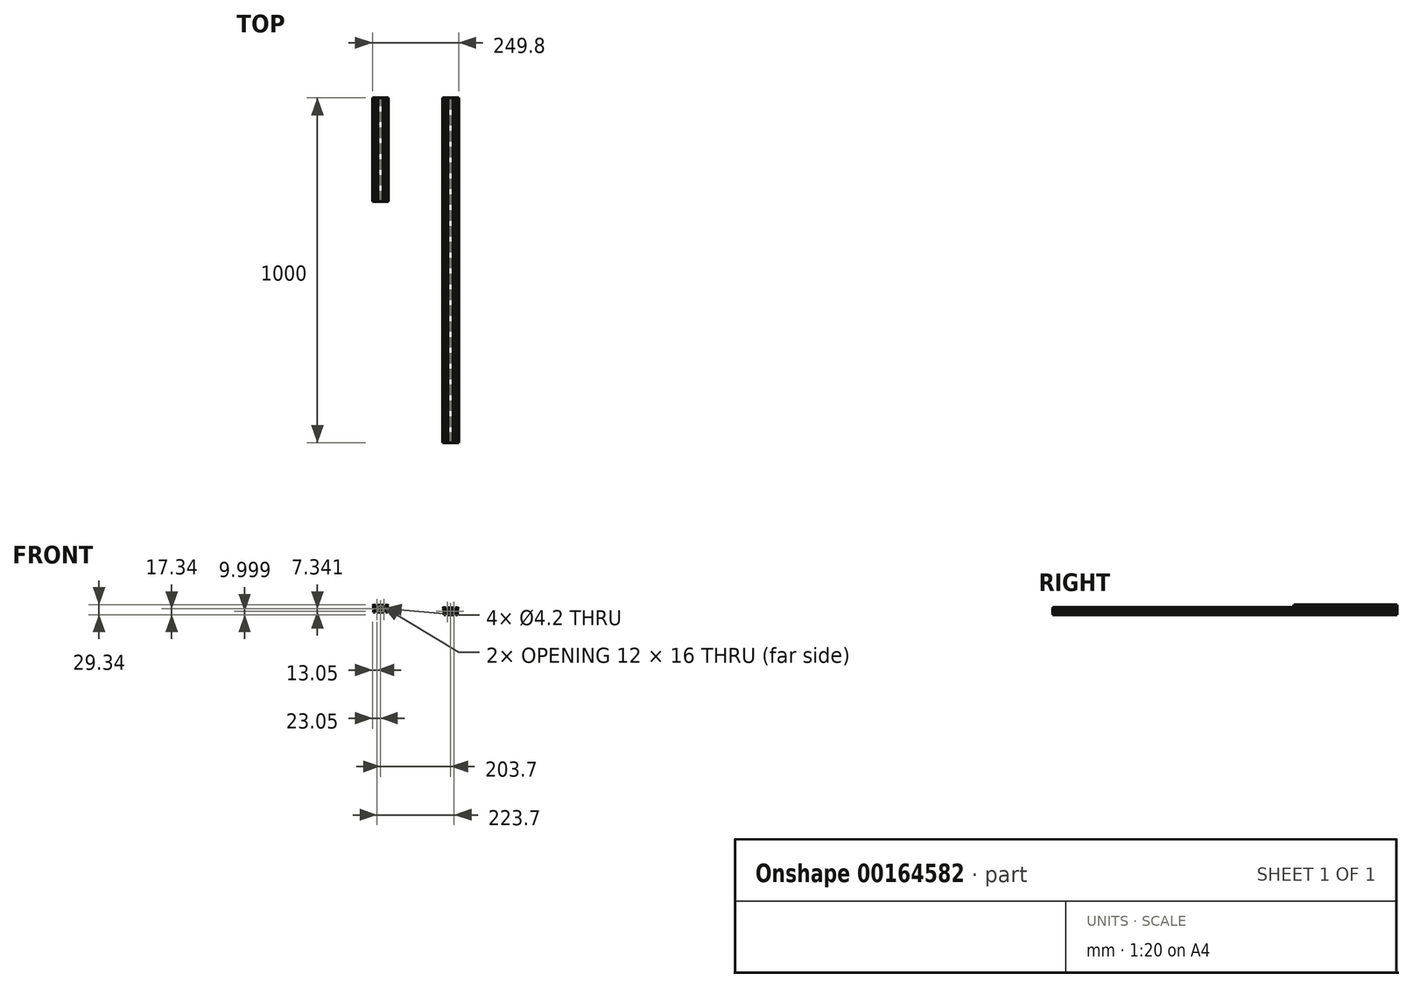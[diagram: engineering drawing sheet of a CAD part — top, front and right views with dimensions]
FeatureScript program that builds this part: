
annotation { "Feature Type Name" : "Feature", "Feature Type Description" : "" }
export const myFeature = defineFeature(function(context is Context, id is Id, definition is map)
    precondition{}
    {
        {
            var Q0;
            Q0=qCreatedBy(makeId("Front.planeOp"),FACE);
            var sketch = newSketch(context, id + "F0", { "sketchPlane" : qUnion([Q0])});
            skLineSegment(sketch, "E0.bottom", {"start": v(-20, 10) * mm, "end": v(-13.5, 10) * mm});
            skLineSegment(sketch, "E0.left", {"start": v(-20, 6.63) * mm, "end": v(-20, 3) * mm});
            skLineSegment(sketch, "E1.bottom", {"start": v(-20.37, 12) * mm, "end": v(-20, 12) * mm});
            skLineSegment(sketch, "E2", {"start": v(-20, 10) * mm, "end": v(-20, 12) * mm});
            skPoint(sketch, "E3.endSnap0", {"position": v(0, -10) * mm});
            skLineSegment(sketch, "E4", {"start": v(-23.05, 9.32) * mm, "end": v(-20.37, 12) * mm});
            skLineSegment(sketch, "E5", {"start": v(-23.05, 9.32) * mm, "end": v(-20.37, 6.63) * mm});
            skLineSegment(sketch, "E6", {"start": v(-20.37, 6.63) * mm, "end": v(-20, 6.63) * mm});
            skLineSegment(sketch, "E7.bottom", {"start": v(-2, 10) * mm, "end": v(-7.5, 10) * mm});
            skLineSegment(sketch, "E7.top", {"start": v(0, 8) * mm, "end": v(-2, 8) * mm});
            skLineSegment(sketch, "E7.left", {"start": v(0, 10) * mm, "end": v(0, 8) * mm});
            skLineSegment(sketch, "E7.right", {"start": v(-7.5, 10) * mm, "end": v(-7.5, 8) * mm});
            skLineSegment(sketch, "E8.top", {"start": v(-16, 8) * mm, "end": v(-13.5, 8) * mm});
            skLineSegment(sketch, "E8.right", {"start": v(-13.5, 10) * mm, "end": v(-13.5, 8) * mm});
            skLineSegment(sketch, "E9.bottom", {"start": v(-20, 10) * mm, "end": v(-18, 10) * mm});
            skLineSegment(sketch, "E9.top", {"start": v(-20, 3) * mm, "end": v(-18, 3) * mm});
            skLineSegment(sketch, "E9.right", {"start": v(-18, 6) * mm, "end": v(-18, 3) * mm});
            skLineSegment(sketch, "E10.top", {"start": v(-20, -3) * mm, "end": v(-18, -3) * mm});
            skLineSegment(sketch, "E11.bottom", {"start": v(-20, -10) * mm, "end": v(-15, -10) * mm});
            skLineSegment(sketch, "E11.left", {"start": v(-20, -10) * mm, "end": v(-20, -8) * mm});
            skLineSegment(sketch, "E11.right", {"start": v(-15, -10) * mm, "end": v(-15, -8) * mm});
            skCircle(sketch, "E12", {"center": v(-10, 0) * mm, "radius": 2.1 * mm});
            skLineSegment(sketch, "E13.bottom", {"start": v(-20, 10) * mm, "end": v(-16, 10) * mm});
            skLineSegment(sketch, "E13.top", {"start": v(-18, 6) * mm, "end": v(-17.41, 6) * mm});
            skLineSegment(sketch, "E13.right", {"start": v(-16, 8) * mm, "end": v(-16, 7.41) * mm});
            skLineSegment(sketch, "E14.right", {"start": v(-4, 8) * mm, "end": v(-4, 7.41) * mm});
            skLineSegment(sketch, "E15.top", {"start": v(-18, -6) * mm, "end": v(-17.41, -6) * mm});
            skLineSegment(sketch, "E15.left", {"start": v(-20, -10) * mm, "end": v(-20, -6) * mm});
            skLineSegment(sketch, "E15.right", {"start": v(-16, -8) * mm, "end": v(-16, -7.41) * mm});
            skLineSegment(sketch, "E16.bottom", {"start": v(-12.59, 4) * mm, "end": v(-7.41, 4) * mm});
            skLineSegment(sketch, "E16.top", {"start": v(-12.59, -4) * mm, "end": v(-7.41, -4) * mm});
            skLineSegment(sketch, "E16.left", {"start": v(-14, 2.59) * mm, "end": v(-14, -2.59) * mm});
            skLineSegment(sketch, "E16.right", {"start": v(-6, 2.59) * mm, "end": v(-6, -2.59) * mm});
            skLineSegment(sketch, "E17", {"start": v(-16, 7.41) * mm, "end": v(-12.59, 4) * mm});
            skLineSegment(sketch, "E18", {"start": v(-17.41, 6) * mm, "end": v(-14, 2.59) * mm});
            skPoint(sketch, "E19.orphan", {"position": v(-16, 6) * mm});
            skLineSegment(sketch, "E20.trimOffspring", {"start": v(-20, 6.63) * mm, "end": v(-20, 6) * mm});
            skLineSegment(sketch, "E21.trimOffspring", {"start": v(-20, -3) * mm, "end": v(-20, -10) * mm});
            skLineSegment(sketch, "E22.trimOffspring", {"start": v(-7.5, 10) * mm, "end": v(-4, 10) * mm});
            skLineSegment(sketch, "E23", {"start": v(-10, 10.96) * mm, "end": v(-10, -11.55) * mm, "construction": true});
            skLineSegment(sketch, "E24.MirrorCS", {"start": v(-4, 7.41) * mm, "end": v(-7.41, 4) * mm});
            skLineSegment(sketch, "E25.MirrorCS", {"start": v(-2.59, 6) * mm, "end": v(-6, 2.59) * mm});
            skLineSegment(sketch, "E26", {"start": v(-2, 8) * mm, "end": v(-2, 6.59) * mm});
            skLineSegment(sketch, "E27", {"start": v(-2.59, 6) * mm, "end": v(-2, 6.59) * mm});
            skLineSegment(sketch, "E28.trimOffspring", {"start": v(-4, 8) * mm, "end": v(-7.5, 8) * mm});
            skPoint(sketch, "E29.orphan", {"position": v(-2, 10) * mm});
            skPoint(sketch, "E30.orphan", {"position": v(-4, 10) * mm});
            skLineSegment(sketch, "E31.trimOffspring", {"start": v(-2, 10) * mm, "end": v(0, 10) * mm});
            skLineSegment(sketch, "E32", {"start": v(-21.49, 0) * mm, "end": v(3.6, 0) * mm, "construction": true});
            skLineSegment(sketch, "E33.MirrorCS", {"start": v(-17.41, -6) * mm, "end": v(-14, -2.59) * mm});
            skLineSegment(sketch, "E34.MirrorCS", {"start": v(-16, -7.41) * mm, "end": v(-12.59, -4) * mm});
            skLineSegment(sketch, "E35.MirrorCS", {"start": v(-4, -8) * mm, "end": v(-4, -7.41) * mm});
            skLineSegment(sketch, "E36.MirrorCS", {"start": v(-2.59, -6) * mm, "end": v(-2, -6.59) * mm});
            skLineSegment(sketch, "E37.MirrorCS", {"start": v(-4, -8) * mm, "end": v(-7.5, -8) * mm});
            skLineSegment(sketch, "E38.MirrorCS", {"start": v(0, -8) * mm, "end": v(-2, -8) * mm});
            skLineSegment(sketch, "E39.MirrorCS", {"start": v(0, -10) * mm, "end": v(0, -8) * mm});
            skLineSegment(sketch, "E40.MirrorCS", {"start": v(-2, -10) * mm, "end": v(-7.5, -10) * mm});
            skLineSegment(sketch, "E41.MirrorCS", {"start": v(-7.5, -10) * mm, "end": v(-7.5, -8) * mm});
            skLineSegment(sketch, "E42.MirrorCS", {"start": v(-2, -8) * mm, "end": v(-2, -6.59) * mm});
            skLineSegment(sketch, "E43.MirrorCS", {"start": v(-7.5, -10) * mm, "end": v(-4, -10) * mm});
            skLineSegment(sketch, "E44.MirrorCS", {"start": v(-2.59, -6) * mm, "end": v(-6, -2.59) * mm});
            skLineSegment(sketch, "E45.MirrorCS", {"start": v(-4, -7.41) * mm, "end": v(-7.41, -4) * mm});
            skLineSegment(sketch, "E46.trimOffspring", {"start": v(-18, -6) * mm, "end": v(-18, -3) * mm});
            skLineSegment(sketch, "E47.trimOffspring", {"start": v(-16, -8) * mm, "end": v(-15, -8) * mm});
            skLineSegment(sketch, "E48.trimOffspring", {"start": v(-7.5, -10) * mm, "end": v(-2, -10) * mm});
            skLineSegment(sketch, "E49.trimOffspring", {"start": v(-7.5, -10) * mm, "end": v(0, -10) * mm});
            skLineSegment(sketch, "E50.MirrorCS", {"start": v(4, -8) * mm, "end": v(4, -7.41) * mm});
            skLineSegment(sketch, "E51.MirrorCS", {"start": v(4, 8) * mm, "end": v(4, 7.41) * mm});
            skLineSegment(sketch, "E52.MirrorCS", {"start": v(20, 6.63) * mm, "end": v(20, 6) * mm});
            skLineSegment(sketch, "E53.MirrorCS", {"start": v(20.37, 6.63) * mm, "end": v(20, 6.63) * mm});
            skLineSegment(sketch, "E54.MirrorCS", {"start": v(16, 8) * mm, "end": v(16, 7.41) * mm});
            skLineSegment(sketch, "E55.MirrorCS", {"start": v(18, 6) * mm, "end": v(17.41, 6) * mm});
            skLineSegment(sketch, "E56.MirrorCS", {"start": v(2.59, 6) * mm, "end": v(2, 6.59) * mm});
            skLineSegment(sketch, "E57.MirrorCS", {"start": v(16, -8) * mm, "end": v(15, -8) * mm});
            skLineSegment(sketch, "E58.MirrorCS", {"start": v(20.37, 12) * mm, "end": v(20, 12) * mm});
            skLineSegment(sketch, "E59.MirrorCS", {"start": v(2, -8) * mm, "end": v(2, -6.59) * mm});
            skLineSegment(sketch, "E60.MirrorCS", {"start": v(18, -6) * mm, "end": v(17.41, -6) * mm});
            skLineSegment(sketch, "E61.MirrorCS", {"start": v(2, 8) * mm, "end": v(2, 6.59) * mm});
            skLineSegment(sketch, "E62.MirrorCS", {"start": v(2.59, -6) * mm, "end": v(2, -6.59) * mm});
            skLineSegment(sketch, "E63.MirrorCS", {"start": v(16, -8) * mm, "end": v(16, -7.41) * mm});
            skLineSegment(sketch, "E64.MirrorCS", {"start": v(20, -10) * mm, "end": v(20, -8) * mm});
            skLineSegment(sketch, "E65.MirrorCS", {"start": v(20, -10) * mm, "end": v(20, -6) * mm});
            skLineSegment(sketch, "E66.MirrorCS", {"start": v(20, 6.63) * mm, "end": v(20, 3) * mm});
            skLineSegment(sketch, "E67.MirrorCS", {"start": v(20, 10) * mm, "end": v(13.5, 10) * mm});
            skLineSegment(sketch, "E68.MirrorCS", {"start": v(20, 10) * mm, "end": v(18, 10) * mm});
            skLineSegment(sketch, "E69.MirrorCS", {"start": v(2, 10) * mm, "end": v(7.5, 10) * mm});
            skLineSegment(sketch, "E70.MirrorCS", {"start": v(7.5, -10) * mm, "end": v(4, -10) * mm});
            skLineSegment(sketch, "E71.MirrorCS", {"start": v(23.05, 9.32) * mm, "end": v(20.37, 6.63) * mm});
            skLineSegment(sketch, "E72.MirrorCS", {"start": v(2, -10) * mm, "end": v(7.5, -10) * mm});
            skLineSegment(sketch, "E73.MirrorCS", {"start": v(16, -7.41) * mm, "end": v(12.59, -4) * mm});
            skLineSegment(sketch, "E74.MirrorCS", {"start": v(7.5, -10) * mm, "end": v(2, -10) * mm});
            skLineSegment(sketch, "E75.MirrorCS", {"start": v(20, -10) * mm, "end": v(15, -10) * mm});
            skLineSegment(sketch, "E76.MirrorCS", {"start": v(7.5, -10) * mm, "end": v(0, -10) * mm});
            skLineSegment(sketch, "E77.MirrorCS", {"start": v(16, 7.41) * mm, "end": v(12.59, 4) * mm});
            skPoint(sketch, "E78.MirrorP", {"position": v(4, 10) * mm});
            skLineSegment(sketch, "E79.MirrorCS", {"start": v(14, 2.59) * mm, "end": v(14, -2.59) * mm});
            skLineSegment(sketch, "E80.MirrorCS", {"start": v(7.5, -10) * mm, "end": v(7.5, -8) * mm});
            skPoint(sketch, "E81.MirrorP", {"position": v(2, 10) * mm});
            skLineSegment(sketch, "E82.MirrorCS", {"start": v(2.59, 6) * mm, "end": v(6, 2.59) * mm});
            skPoint(sketch, "E83.MirrorP", {"position": v(16, 6) * mm});
            skLineSegment(sketch, "E84.MirrorCS", {"start": v(17.41, -6) * mm, "end": v(14, -2.59) * mm});
            skLineSegment(sketch, "E85.MirrorCS", {"start": v(18, 6) * mm, "end": v(18, 3) * mm});
            skLineSegment(sketch, "E86.MirrorCS", {"start": v(10, 10.96) * mm, "end": v(10, -11.55) * mm, "construction": true});
            skLineSegment(sketch, "E87.MirrorCS", {"start": v(20, -3) * mm, "end": v(20, -10) * mm});
            skLineSegment(sketch, "E88.MirrorCS", {"start": v(13.5, 10) * mm, "end": v(13.5, 8) * mm});
            skLineSegment(sketch, "E89.MirrorCS", {"start": v(20, 3) * mm, "end": v(18, 3) * mm});
            skLineSegment(sketch, "E90.MirrorCS", {"start": v(23.05, 9.32) * mm, "end": v(20.37, 12) * mm});
            skLineSegment(sketch, "E91.MirrorCS", {"start": v(12.59, 4) * mm, "end": v(7.41, 4) * mm});
            skLineSegment(sketch, "E92.MirrorCS", {"start": v(4, -7.41) * mm, "end": v(7.41, -4) * mm});
            skLineSegment(sketch, "E93.MirrorCS", {"start": v(0, 8) * mm, "end": v(2, 8) * mm});
            skLineSegment(sketch, "E94.MirrorCS", {"start": v(2, 10) * mm, "end": v(0, 10) * mm});
            skLineSegment(sketch, "E95.MirrorCS", {"start": v(4, -8) * mm, "end": v(7.5, -8) * mm});
            skCircle(sketch, "E96.MirrorC", {"center": v(10, 0) * mm, "radius": 2.1 * mm});
            skLineSegment(sketch, "E97.MirrorCS", {"start": v(17.41, 6) * mm, "end": v(14, 2.59) * mm});
            skLineSegment(sketch, "E98.MirrorCS", {"start": v(12.59, -4) * mm, "end": v(7.41, -4) * mm});
            skLineSegment(sketch, "E99.MirrorCS", {"start": v(6, 2.59) * mm, "end": v(6, -2.59) * mm});
            skLineSegment(sketch, "E100.MirrorCS", {"start": v(4, 7.41) * mm, "end": v(7.41, 4) * mm});
            skLineSegment(sketch, "E101.MirrorCS", {"start": v(7.5, 10) * mm, "end": v(4, 10) * mm});
            skLineSegment(sketch, "E102.MirrorCS", {"start": v(0, -8) * mm, "end": v(2, -8) * mm});
            skLineSegment(sketch, "E103.MirrorCS", {"start": v(7.5, 10) * mm, "end": v(7.5, 8) * mm});
            skLineSegment(sketch, "E104.MirrorCS", {"start": v(16, 8) * mm, "end": v(13.5, 8) * mm});
            skLineSegment(sketch, "E105.MirrorCS", {"start": v(4, 8) * mm, "end": v(7.5, 8) * mm});
            skLineSegment(sketch, "E106.MirrorCS", {"start": v(2.59, -6) * mm, "end": v(6, -2.59) * mm});
            skLineSegment(sketch, "E107.MirrorCS", {"start": v(18, -6) * mm, "end": v(18, -3) * mm});
            skLineSegment(sketch, "E108.MirrorCS", {"start": v(20, 10) * mm, "end": v(20, 12) * mm});
            skLineSegment(sketch, "E109.MirrorCS", {"start": v(15, -10) * mm, "end": v(15, -8) * mm});
            skLineSegment(sketch, "E110.MirrorCS", {"start": v(20, 10) * mm, "end": v(16, 10) * mm});
            skLineSegment(sketch, "E111.MirrorCS", {"start": v(20, -3) * mm, "end": v(18, -3) * mm});
            skSolve(sketch);
        }
        {
            var Q0;
            Q0 = qSketchRegion(id + "F0", true);
            extrude(context, id + "F1", {"entities" : qUnion([Q0]), "offsetDistance" : 25 * mm, "depth" : 300 * mm});
        }
        {
            var Q0;
            Q0=qCreatedBy(makeId("Front.planeOp"),FACE);
            var sketch = newSketch(context, id + "F2", { "sketchPlane" : qUnion([Q0])});
            skLineSegment(sketch, "E112.bottom", {"start": v(183.7, 2.66) * mm, "end": v(190.2, 2.66) * mm});
            skLineSegment(sketch, "E112.left", {"start": v(183.7, -0.71) * mm, "end": v(183.7, -4.34) * mm});
            skLineSegment(sketch, "E113.bottom", {"start": v(183.33, 4.66) * mm, "end": v(183.7, 4.66) * mm});
            skLineSegment(sketch, "E114", {"start": v(183.7, 2.66) * mm, "end": v(183.7, 4.66) * mm});
            skPoint(sketch, "E115.endSnap0", {"position": v(203.7, -17.34) * mm});
            skLineSegment(sketch, "E116", {"start": v(180.65, 1.97) * mm, "end": v(183.33, 4.66) * mm});
            skLineSegment(sketch, "E117", {"start": v(180.65, 1.97) * mm, "end": v(183.33, -0.71) * mm});
            skLineSegment(sketch, "E118", {"start": v(183.33, -0.71) * mm, "end": v(183.7, -0.71) * mm});
            skLineSegment(sketch, "E119.bottom", {"start": v(201.7, 2.66) * mm, "end": v(196.2, 2.66) * mm});
            skLineSegment(sketch, "E119.top", {"start": v(203.7, 0.66) * mm, "end": v(201.7, 0.66) * mm});
            skLineSegment(sketch, "E119.left", {"start": v(203.7, 2.66) * mm, "end": v(203.7, 0.66) * mm});
            skLineSegment(sketch, "E119.right", {"start": v(196.2, 2.66) * mm, "end": v(196.2, 0.66) * mm});
            skLineSegment(sketch, "E120.top", {"start": v(187.7, 0.66) * mm, "end": v(190.2, 0.66) * mm});
            skLineSegment(sketch, "E120.right", {"start": v(190.2, 2.66) * mm, "end": v(190.2, 0.66) * mm});
            skLineSegment(sketch, "E121.bottom", {"start": v(183.7, 2.66) * mm, "end": v(185.7, 2.66) * mm});
            skLineSegment(sketch, "E121.top", {"start": v(183.7, -4.34) * mm, "end": v(185.7, -4.34) * mm});
            skLineSegment(sketch, "E121.right", {"start": v(185.7, -1.34) * mm, "end": v(185.7, -4.34) * mm});
            skLineSegment(sketch, "E122.top", {"start": v(183.7, -10.34) * mm, "end": v(185.7, -10.34) * mm});
            skLineSegment(sketch, "E123.bottom", {"start": v(183.7, -17.34) * mm, "end": v(188.7, -17.34) * mm});
            skLineSegment(sketch, "E123.left", {"start": v(183.7, -17.34) * mm, "end": v(183.7, -15.34) * mm});
            skLineSegment(sketch, "E123.right", {"start": v(188.7, -17.34) * mm, "end": v(188.7, -15.34) * mm});
            skCircle(sketch, "E124", {"center": v(193.7, -7.34) * mm, "radius": 2.1 * mm});
            skLineSegment(sketch, "E125.bottom", {"start": v(183.7, 2.66) * mm, "end": v(187.7, 2.66) * mm});
            skLineSegment(sketch, "E125.top", {"start": v(185.7, -1.34) * mm, "end": v(186.29, -1.34) * mm});
            skLineSegment(sketch, "E125.right", {"start": v(187.7, 0.66) * mm, "end": v(187.7, 0.07) * mm});
            skLineSegment(sketch, "E126.right", {"start": v(199.7, 0.66) * mm, "end": v(199.7, 0.07) * mm});
            skLineSegment(sketch, "E127.top", {"start": v(185.7, -13.34) * mm, "end": v(186.29, -13.34) * mm});
            skLineSegment(sketch, "E127.left", {"start": v(183.7, -17.34) * mm, "end": v(183.7, -13.34) * mm});
            skLineSegment(sketch, "E127.right", {"start": v(187.7, -15.34) * mm, "end": v(187.7, -14.76) * mm});
            skLineSegment(sketch, "E128.bottom", {"start": v(191.11, -3.34) * mm, "end": v(196.29, -3.34) * mm});
            skLineSegment(sketch, "E128.top", {"start": v(191.11, -11.34) * mm, "end": v(196.29, -11.34) * mm});
            skLineSegment(sketch, "E128.left", {"start": v(189.7, -4.76) * mm, "end": v(189.7, -9.93) * mm});
            skLineSegment(sketch, "E128.right", {"start": v(197.7, -4.76) * mm, "end": v(197.7, -9.93) * mm});
            skLineSegment(sketch, "E129", {"start": v(187.7, 0.07) * mm, "end": v(191.11, -3.34) * mm});
            skLineSegment(sketch, "E130", {"start": v(186.29, -1.34) * mm, "end": v(189.7, -4.76) * mm});
            skPoint(sketch, "E131.orphan", {"position": v(187.7, -1.34) * mm});
            skLineSegment(sketch, "E132.trimOffspring", {"start": v(183.7, -0.71) * mm, "end": v(183.7, -1.34) * mm});
            skLineSegment(sketch, "E133.trimOffspring", {"start": v(183.7, -10.34) * mm, "end": v(183.7, -17.34) * mm});
            skLineSegment(sketch, "E134.trimOffspring", {"start": v(196.2, 2.66) * mm, "end": v(199.7, 2.66) * mm});
            skLineSegment(sketch, "E135", {"start": v(193.7, 3.62) * mm, "end": v(193.7, -18.9) * mm, "construction": true});
            skLineSegment(sketch, "E136.MirrorCS", {"start": v(199.7, 0.07) * mm, "end": v(196.29, -3.34) * mm});
            skLineSegment(sketch, "E137.MirrorCS", {"start": v(201.11, -1.34) * mm, "end": v(197.7, -4.76) * mm});
            skLineSegment(sketch, "E138", {"start": v(201.7, 0.66) * mm, "end": v(201.7, -0.76) * mm});
            skLineSegment(sketch, "E139", {"start": v(201.11, -1.34) * mm, "end": v(201.7, -0.76) * mm});
            skLineSegment(sketch, "E140.trimOffspring", {"start": v(199.7, 0.66) * mm, "end": v(196.2, 0.66) * mm});
            skPoint(sketch, "E141.orphan", {"position": v(201.7, 2.66) * mm});
            skPoint(sketch, "E142.orphan", {"position": v(199.7, 2.66) * mm});
            skLineSegment(sketch, "E143.trimOffspring", {"start": v(201.7, 2.66) * mm, "end": v(203.7, 2.66) * mm});
            skLineSegment(sketch, "E144", {"start": v(182.21, -7.34) * mm, "end": v(207.3, -7.34) * mm, "construction": true});
            skLineSegment(sketch, "E145.MirrorCS", {"start": v(186.29, -13.34) * mm, "end": v(189.7, -9.93) * mm});
            skLineSegment(sketch, "E146.MirrorCS", {"start": v(187.7, -14.76) * mm, "end": v(191.11, -11.34) * mm});
            skLineSegment(sketch, "E147.MirrorCS", {"start": v(199.7, -15.34) * mm, "end": v(199.7, -14.76) * mm});
            skLineSegment(sketch, "E148.MirrorCS", {"start": v(201.11, -13.34) * mm, "end": v(201.7, -13.93) * mm});
            skLineSegment(sketch, "E149.MirrorCS", {"start": v(199.7, -15.34) * mm, "end": v(196.2, -15.34) * mm});
            skLineSegment(sketch, "E150.MirrorCS", {"start": v(203.7, -15.34) * mm, "end": v(201.7, -15.34) * mm});
            skLineSegment(sketch, "E151.MirrorCS", {"start": v(203.7, -17.34) * mm, "end": v(203.7, -15.34) * mm});
            skLineSegment(sketch, "E152.MirrorCS", {"start": v(201.7, -17.34) * mm, "end": v(196.2, -17.34) * mm});
            skLineSegment(sketch, "E153.MirrorCS", {"start": v(196.2, -17.34) * mm, "end": v(196.2, -15.34) * mm});
            skLineSegment(sketch, "E154.MirrorCS", {"start": v(201.7, -15.34) * mm, "end": v(201.7, -13.93) * mm});
            skLineSegment(sketch, "E155.MirrorCS", {"start": v(196.2, -17.34) * mm, "end": v(199.7, -17.34) * mm});
            skLineSegment(sketch, "E156.MirrorCS", {"start": v(201.11, -13.34) * mm, "end": v(197.7, -9.93) * mm});
            skLineSegment(sketch, "E157.MirrorCS", {"start": v(199.7, -14.76) * mm, "end": v(196.29, -11.34) * mm});
            skLineSegment(sketch, "E158.trimOffspring", {"start": v(185.7, -13.34) * mm, "end": v(185.7, -10.34) * mm});
            skLineSegment(sketch, "E159.trimOffspring", {"start": v(187.7, -15.34) * mm, "end": v(188.7, -15.34) * mm});
            skLineSegment(sketch, "E160.trimOffspring", {"start": v(196.2, -17.34) * mm, "end": v(201.7, -17.34) * mm});
            skLineSegment(sketch, "E161.trimOffspring", {"start": v(196.2, -17.34) * mm, "end": v(203.7, -17.34) * mm});
            skLineSegment(sketch, "E162.MirrorCS", {"start": v(207.7, -15.34) * mm, "end": v(207.7, -14.76) * mm});
            skLineSegment(sketch, "E163.MirrorCS", {"start": v(207.7, 0.66) * mm, "end": v(207.7, 0.07) * mm});
            skLineSegment(sketch, "E164.MirrorCS", {"start": v(223.7, -0.71) * mm, "end": v(223.7, -1.34) * mm});
            skLineSegment(sketch, "E165.MirrorCS", {"start": v(224.07, -0.71) * mm, "end": v(223.7, -0.71) * mm});
            skLineSegment(sketch, "E166.MirrorCS", {"start": v(219.7, 0.66) * mm, "end": v(219.7, 0.07) * mm});
            skLineSegment(sketch, "E167.MirrorCS", {"start": v(221.7, -1.34) * mm, "end": v(221.11, -1.34) * mm});
            skLineSegment(sketch, "E168.MirrorCS", {"start": v(206.29, -1.34) * mm, "end": v(205.7, -0.76) * mm});
            skLineSegment(sketch, "E169.MirrorCS", {"start": v(219.7, -15.34) * mm, "end": v(218.7, -15.34) * mm});
            skLineSegment(sketch, "E170.MirrorCS", {"start": v(224.07, 4.66) * mm, "end": v(223.7, 4.66) * mm});
            skLineSegment(sketch, "E171.MirrorCS", {"start": v(205.7, -15.34) * mm, "end": v(205.7, -13.93) * mm});
            skLineSegment(sketch, "E172.MirrorCS", {"start": v(221.7, -13.34) * mm, "end": v(221.11, -13.34) * mm});
            skLineSegment(sketch, "E173.MirrorCS", {"start": v(205.7, 0.66) * mm, "end": v(205.7, -0.76) * mm});
            skLineSegment(sketch, "E174.MirrorCS", {"start": v(206.29, -13.34) * mm, "end": v(205.7, -13.93) * mm});
            skLineSegment(sketch, "E175.MirrorCS", {"start": v(219.7, -15.34) * mm, "end": v(219.7, -14.76) * mm});
            skLineSegment(sketch, "E176.MirrorCS", {"start": v(223.7, -17.34) * mm, "end": v(223.7, -15.34) * mm});
            skLineSegment(sketch, "E177.MirrorCS", {"start": v(223.7, -17.34) * mm, "end": v(223.7, -13.34) * mm});
            skLineSegment(sketch, "E178.MirrorCS", {"start": v(223.7, -0.71) * mm, "end": v(223.7, -4.34) * mm});
            skLineSegment(sketch, "E179.MirrorCS", {"start": v(223.7, 2.66) * mm, "end": v(217.2, 2.66) * mm});
            skLineSegment(sketch, "E180.MirrorCS", {"start": v(223.7, 2.66) * mm, "end": v(221.7, 2.66) * mm});
            skLineSegment(sketch, "E181.MirrorCS", {"start": v(205.7, 2.66) * mm, "end": v(211.2, 2.66) * mm});
            skLineSegment(sketch, "E182.MirrorCS", {"start": v(211.2, -17.34) * mm, "end": v(207.7, -17.34) * mm});
            skLineSegment(sketch, "E183.MirrorCS", {"start": v(226.75, 1.97) * mm, "end": v(224.07, -0.71) * mm});
            skLineSegment(sketch, "E184.MirrorCS", {"start": v(205.7, -17.34) * mm, "end": v(211.2, -17.34) * mm});
            skLineSegment(sketch, "E185.MirrorCS", {"start": v(219.7, -14.76) * mm, "end": v(216.29, -11.34) * mm});
            skLineSegment(sketch, "E186.MirrorCS", {"start": v(211.2, -17.34) * mm, "end": v(205.7, -17.34) * mm});
            skLineSegment(sketch, "E187.MirrorCS", {"start": v(223.7, -17.34) * mm, "end": v(218.7, -17.34) * mm});
            skLineSegment(sketch, "E188.MirrorCS", {"start": v(211.2, -17.34) * mm, "end": v(203.7, -17.34) * mm});
            skLineSegment(sketch, "E189.MirrorCS", {"start": v(219.7, 0.07) * mm, "end": v(216.29, -3.34) * mm});
            skPoint(sketch, "E190.MirrorP", {"position": v(207.7, 2.66) * mm});
            skLineSegment(sketch, "E191.MirrorCS", {"start": v(217.7, -4.76) * mm, "end": v(217.7, -9.93) * mm});
            skLineSegment(sketch, "E192.MirrorCS", {"start": v(211.2, -17.34) * mm, "end": v(211.2, -15.34) * mm});
            skPoint(sketch, "E193.MirrorP", {"position": v(205.7, 2.66) * mm});
            skLineSegment(sketch, "E194.MirrorCS", {"start": v(206.29, -1.34) * mm, "end": v(209.7, -4.76) * mm});
            skPoint(sketch, "E195.MirrorP", {"position": v(219.7, -1.34) * mm});
            skLineSegment(sketch, "E196.MirrorCS", {"start": v(221.11, -13.34) * mm, "end": v(217.7, -9.93) * mm});
            skLineSegment(sketch, "E197.MirrorCS", {"start": v(221.7, -1.34) * mm, "end": v(221.7, -4.34) * mm});
            skLineSegment(sketch, "E198.MirrorCS", {"start": v(213.7, 3.62) * mm, "end": v(213.7, -18.9) * mm, "construction": true});
            skLineSegment(sketch, "E199.MirrorCS", {"start": v(223.7, -10.34) * mm, "end": v(223.7, -17.34) * mm});
            skLineSegment(sketch, "E200.MirrorCS", {"start": v(217.2, 2.66) * mm, "end": v(217.2, 0.66) * mm});
            skLineSegment(sketch, "E201.MirrorCS", {"start": v(223.7, -4.34) * mm, "end": v(221.7, -4.34) * mm});
            skLineSegment(sketch, "E202.MirrorCS", {"start": v(226.75, 1.97) * mm, "end": v(224.07, 4.66) * mm});
            skLineSegment(sketch, "E203.MirrorCS", {"start": v(216.29, -3.34) * mm, "end": v(211.11, -3.34) * mm});
            skLineSegment(sketch, "E204.MirrorCS", {"start": v(207.7, -14.76) * mm, "end": v(211.11, -11.34) * mm});
            skLineSegment(sketch, "E205.MirrorCS", {"start": v(203.7, 0.66) * mm, "end": v(205.7, 0.66) * mm});
            skLineSegment(sketch, "E206.MirrorCS", {"start": v(205.7, 2.66) * mm, "end": v(203.7, 2.66) * mm});
            skLineSegment(sketch, "E207.MirrorCS", {"start": v(207.7, -15.34) * mm, "end": v(211.2, -15.34) * mm});
            skCircle(sketch, "E208.MirrorC", {"center": v(213.7, -7.34) * mm, "radius": 2.1 * mm});
            skLineSegment(sketch, "E209.MirrorCS", {"start": v(221.11, -1.34) * mm, "end": v(217.7, -4.76) * mm});
            skLineSegment(sketch, "E210.MirrorCS", {"start": v(216.29, -11.34) * mm, "end": v(211.11, -11.34) * mm});
            skLineSegment(sketch, "E211.MirrorCS", {"start": v(209.7, -4.76) * mm, "end": v(209.7, -9.93) * mm});
            skLineSegment(sketch, "E212.MirrorCS", {"start": v(207.7, 0.07) * mm, "end": v(211.11, -3.34) * mm});
            skLineSegment(sketch, "E213.MirrorCS", {"start": v(211.2, 2.66) * mm, "end": v(207.7, 2.66) * mm});
            skLineSegment(sketch, "E214.MirrorCS", {"start": v(203.7, -15.34) * mm, "end": v(205.7, -15.34) * mm});
            skLineSegment(sketch, "E215.MirrorCS", {"start": v(211.2, 2.66) * mm, "end": v(211.2, 0.66) * mm});
            skLineSegment(sketch, "E216.MirrorCS", {"start": v(219.7, 0.66) * mm, "end": v(217.2, 0.66) * mm});
            skLineSegment(sketch, "E217.MirrorCS", {"start": v(207.7, 0.66) * mm, "end": v(211.2, 0.66) * mm});
            skLineSegment(sketch, "E218.MirrorCS", {"start": v(206.29, -13.34) * mm, "end": v(209.7, -9.93) * mm});
            skLineSegment(sketch, "E219.MirrorCS", {"start": v(221.7, -13.34) * mm, "end": v(221.7, -10.34) * mm});
            skLineSegment(sketch, "E220.MirrorCS", {"start": v(223.7, 2.66) * mm, "end": v(223.7, 4.66) * mm});
            skLineSegment(sketch, "E221.MirrorCS", {"start": v(218.7, -17.34) * mm, "end": v(218.7, -15.34) * mm});
            skLineSegment(sketch, "E222.MirrorCS", {"start": v(223.7, 2.66) * mm, "end": v(219.7, 2.66) * mm});
            skLineSegment(sketch, "E223.MirrorCS", {"start": v(223.7, -10.34) * mm, "end": v(221.7, -10.34) * mm});
            skSolve(sketch);
        }
        {
            var Q0;
            Q0 = qSketchRegion(id + "F2", true);
            extrude(context, id + "F3", {"entities" : qUnion([Q0]), "depth" : 1000 * mm, "offsetDistance" : 25 * mm});
        }
    });
